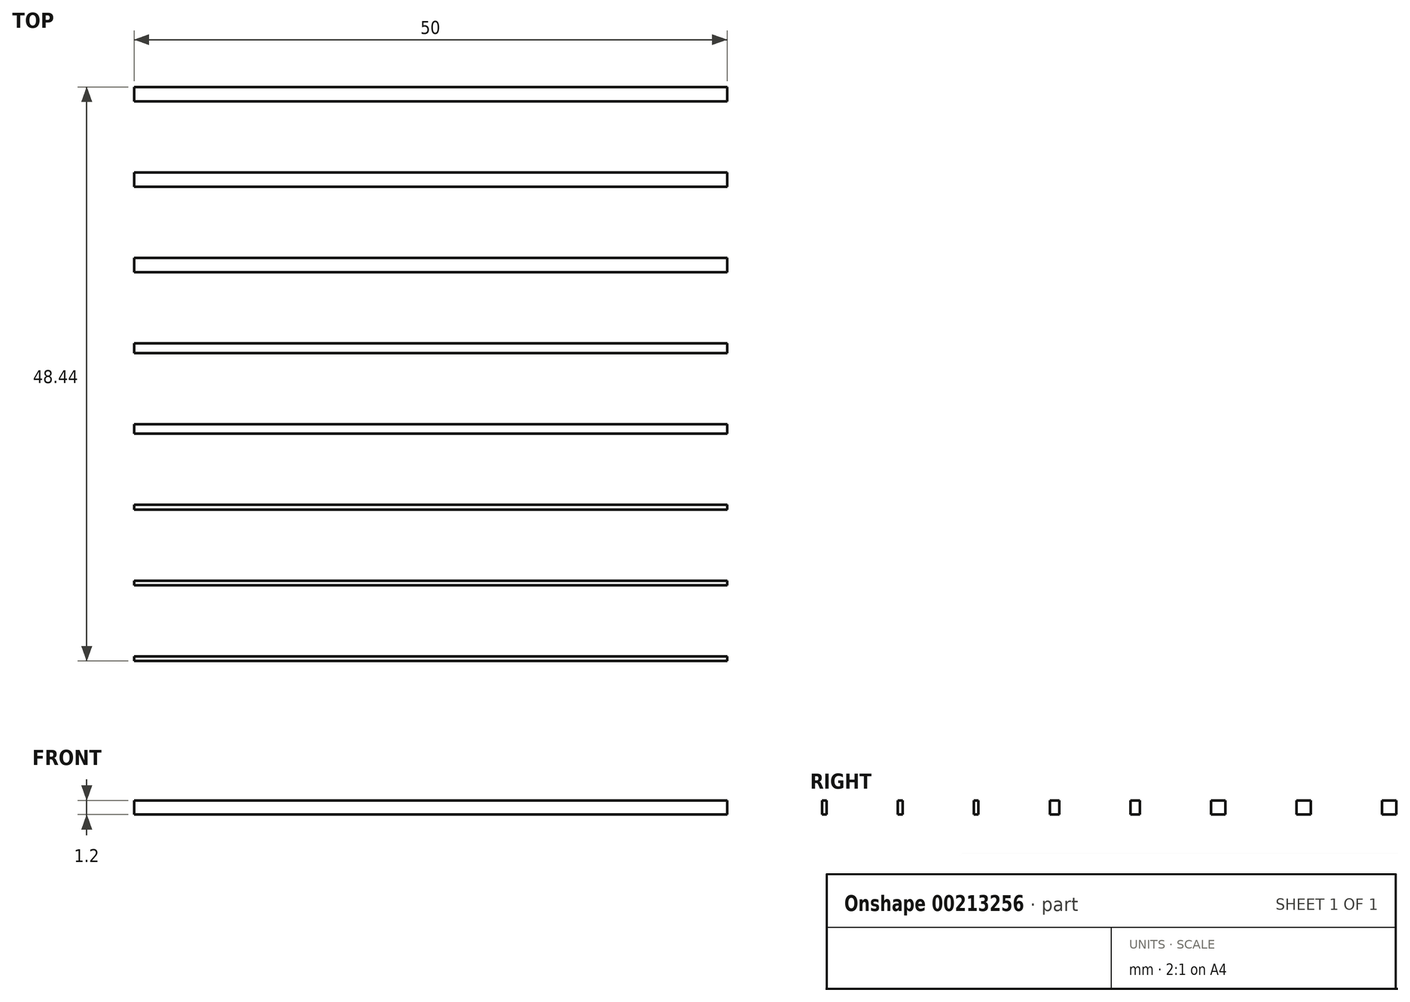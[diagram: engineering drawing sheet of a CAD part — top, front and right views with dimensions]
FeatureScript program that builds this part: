
annotation { "Feature Type Name" : "Feature", "Feature Type Description" : "" }
export const myFeature = defineFeature(function(context is Context, id is Id, definition is map)
    precondition{}
    {
        {
            var Q0;
            Q0=qCreatedBy(makeId("Top.planeOp"),FACE);
            var sketch = newSketch(context, id + "F0", { "sketchPlane" : qUnion([Q0])});
            skLineSegment(sketch, "E0.bottom", {"start": v(0, 0) * mm, "end": v(50, 0) * mm});
            skLineSegment(sketch, "E0.top", {"start": v(0, 0.39) * mm, "end": v(50, 0.39) * mm});
            skLineSegment(sketch, "E0.left", {"start": v(0, 0) * mm, "end": v(0, 0.39) * mm});
            skLineSegment(sketch, "E0.right", {"start": v(50, 0) * mm, "end": v(50, 0.39) * mm});
            skLineSegment(sketch, "E1.bottom", {"start": v(0, 6.79) * mm, "end": v(50, 6.79) * mm});
            skLineSegment(sketch, "E1.top", {"start": v(0, 6.39) * mm, "end": v(50, 6.39) * mm});
            skLineSegment(sketch, "E1.left", {"start": v(0, 6.79) * mm, "end": v(0, 6.39) * mm});
            skLineSegment(sketch, "E1.right", {"start": v(50, 6.79) * mm, "end": v(50, 6.39) * mm});
            skLineSegment(sketch, "E2.bottom", {"start": v(0, 13.2) * mm, "end": v(50, 13.2) * mm});
            skLineSegment(sketch, "E2.top", {"start": v(0, 12.79) * mm, "end": v(50, 12.79) * mm});
            skLineSegment(sketch, "E2.left", {"start": v(0, 13.2) * mm, "end": v(0, 12.79) * mm});
            skLineSegment(sketch, "E2.right", {"start": v(50, 13.2) * mm, "end": v(50, 12.79) * mm});
            skLineSegment(sketch, "E3.bottom", {"start": v(0, 19.2) * mm, "end": v(50, 19.2) * mm});
            skLineSegment(sketch, "E3.top", {"start": v(0, 20) * mm, "end": v(50, 20) * mm});
            skLineSegment(sketch, "E3.left", {"start": v(0, 19.2) * mm, "end": v(0, 20) * mm});
            skLineSegment(sketch, "E3.right", {"start": v(50, 19.2) * mm, "end": v(50, 20) * mm});
            skLineSegment(sketch, "E4.bottom", {"start": v(0, 26) * mm, "end": v(50, 26) * mm});
            skLineSegment(sketch, "E4.top", {"start": v(0, 26.8) * mm, "end": v(50, 26.8) * mm});
            skLineSegment(sketch, "E4.left", {"start": v(0, 26) * mm, "end": v(0, 26.8) * mm});
            skLineSegment(sketch, "E4.right", {"start": v(50, 26) * mm, "end": v(50, 26.8) * mm});
            skLineSegment(sketch, "E5.bottom", {"start": v(0, 34) * mm, "end": v(50, 34) * mm});
            skLineSegment(sketch, "E5.top", {"start": v(0, 32.8) * mm, "end": v(50, 32.8) * mm});
            skLineSegment(sketch, "E5.left", {"start": v(0, 34) * mm, "end": v(0, 32.8) * mm});
            skLineSegment(sketch, "E5.right", {"start": v(50, 34) * mm, "end": v(50, 32.8) * mm});
            skLineSegment(sketch, "E6.bottom", {"start": v(0, 41.22) * mm, "end": v(50, 41.22) * mm});
            skLineSegment(sketch, "E6.top", {"start": v(0, 40) * mm, "end": v(50, 40) * mm});
            skLineSegment(sketch, "E6.left", {"start": v(0, 41.22) * mm, "end": v(0, 40) * mm});
            skLineSegment(sketch, "E6.right", {"start": v(50, 41.22) * mm, "end": v(50, 40) * mm});
            skLineSegment(sketch, "E7.bottom", {"start": v(0, 48.44) * mm, "end": v(50, 48.44) * mm});
            skLineSegment(sketch, "E7.top", {"start": v(0, 47.22) * mm, "end": v(50, 47.22) * mm});
            skLineSegment(sketch, "E7.left", {"start": v(0, 48.44) * mm, "end": v(0, 47.22) * mm});
            skLineSegment(sketch, "E7.right", {"start": v(50, 48.44) * mm, "end": v(50, 47.22) * mm});
            skLineSegment(sketch, "E8", {"start": v(0, 47.22) * mm, "end": v(0, 41.22) * mm, "construction": true});
            skLineSegment(sketch, "E9", {"start": v(0, 40) * mm, "end": v(0, 34) * mm, "construction": true});
            skLineSegment(sketch, "E10", {"start": v(0, 32.8) * mm, "end": v(0, 26.8) * mm, "construction": true});
            skLineSegment(sketch, "E11", {"start": v(0, 26) * mm, "end": v(0, 20) * mm, "construction": true});
            skLineSegment(sketch, "E12", {"start": v(0, 19.2) * mm, "end": v(0, 13.2) * mm, "construction": true});
            skLineSegment(sketch, "E13", {"start": v(0, 12.79) * mm, "end": v(0, 6.79) * mm, "construction": true});
            skLineSegment(sketch, "E14", {"start": v(0, 6.39) * mm, "end": v(0, 0.39) * mm, "construction": true});
            skSolve(sketch);
        }
        {
            var Q0;
            Q0 = qSketchRegion(id + "F0", true);
            extrude(context, id + "F1", {"entities" : qUnion([Q0]), "depth" : 1.2 * mm});
        }
    });
